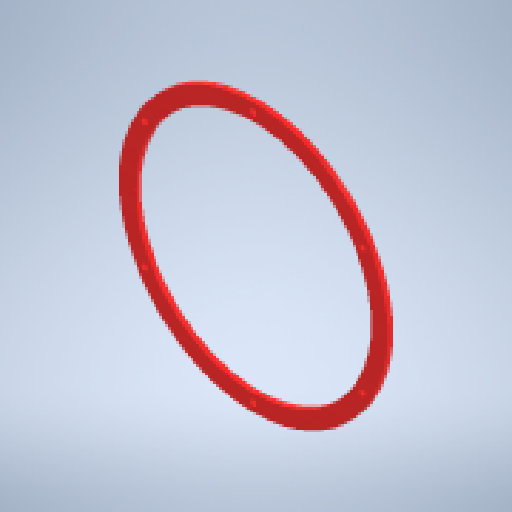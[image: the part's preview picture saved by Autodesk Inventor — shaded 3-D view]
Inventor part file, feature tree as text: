
AUTODESK INVENTOR PART (.ipt)
format: ipt  version: 2024 (Build 280153000, 153)  size: 206,848 bytes
history: native  units: mm
features: sketch x4, extrude x3, pattern_circular x2, other x1, hole x1
ambient origin geometry x8: Origin, YZ Plane, XZ Plane, XY Plane, X Axis, Y Axis, Z Axis, Center Point
bodies: Body1 (feature_tree)
feature tree (11):
  other  "ソリッド1"
  extrude  "押し出し1"  Depth=160.0mm
  hole  "穴1"  [1 undecoded]
  pattern_circular  "円形状パターン1"  [2 undecoded]
  extrude  "押し出し2"  Depth=75.0mm
  extrude  "押し出し3"  Depth=60.0mm TaperAngle=360.0deg
  pattern_circular  "円形状パターン2"  [2 undecoded]
  sketch  "スケッチ1"
  sketch  "スケッチ2"
  sketch  "スケッチ3"
  sketch  "スケッチ4"
note: 5 required parameter values undecoded (feature->parameter linkage not recoverable at this tier; creation-order binding heuristic only, values carry confidence <= 0.55)
